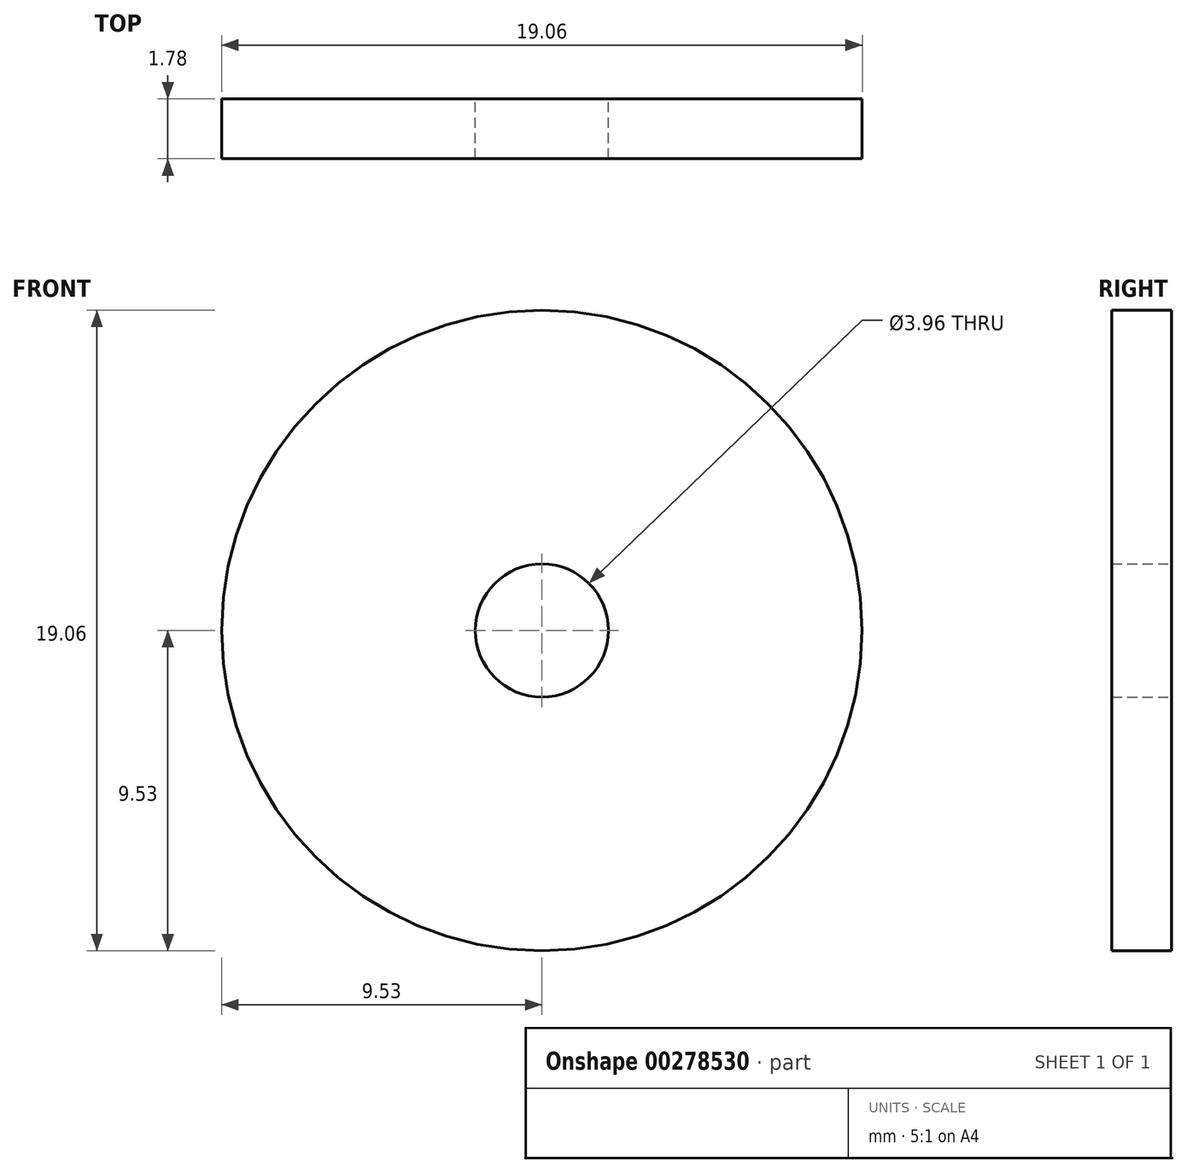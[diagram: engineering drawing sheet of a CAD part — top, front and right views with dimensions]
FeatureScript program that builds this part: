
annotation { "Feature Type Name" : "Feature", "Feature Type Description" : "" }
export const myFeature = defineFeature(function(context is Context, id is Id, definition is map)
    precondition{}
    {
        {
            var Q0;
            Q0=qCreatedBy(makeId("Front.planeOp"),FACE);
            var sketch = newSketch(context, id + "F0", { "sketchPlane" : qUnion([Q0])});
            skCircle(sketch, "E0", {"center": v(0, 0) * mm, "radius": 1.98 * mm});
            skCircle(sketch, "E1", {"center": v(0, 0) * mm, "radius": 9.53 * mm});
            skSolve(sketch);
        }
        {
            var Q0;
            Q0=makeQuery(id+"F0.imprint","IMPRINT",FACE,{"disambiguationData":[TD([[makeQuery(id+"F0.imprint","IMPRINT",EDGE,{"derivedFrom":sQuery(id+"F0.wireOp",EDGE,"E0")}),-1.0]])]});
            extrude(context, id + "F1", {"entities" : qUnion([Q0]), "depth" : 1.78 * mm});
        }
    });
